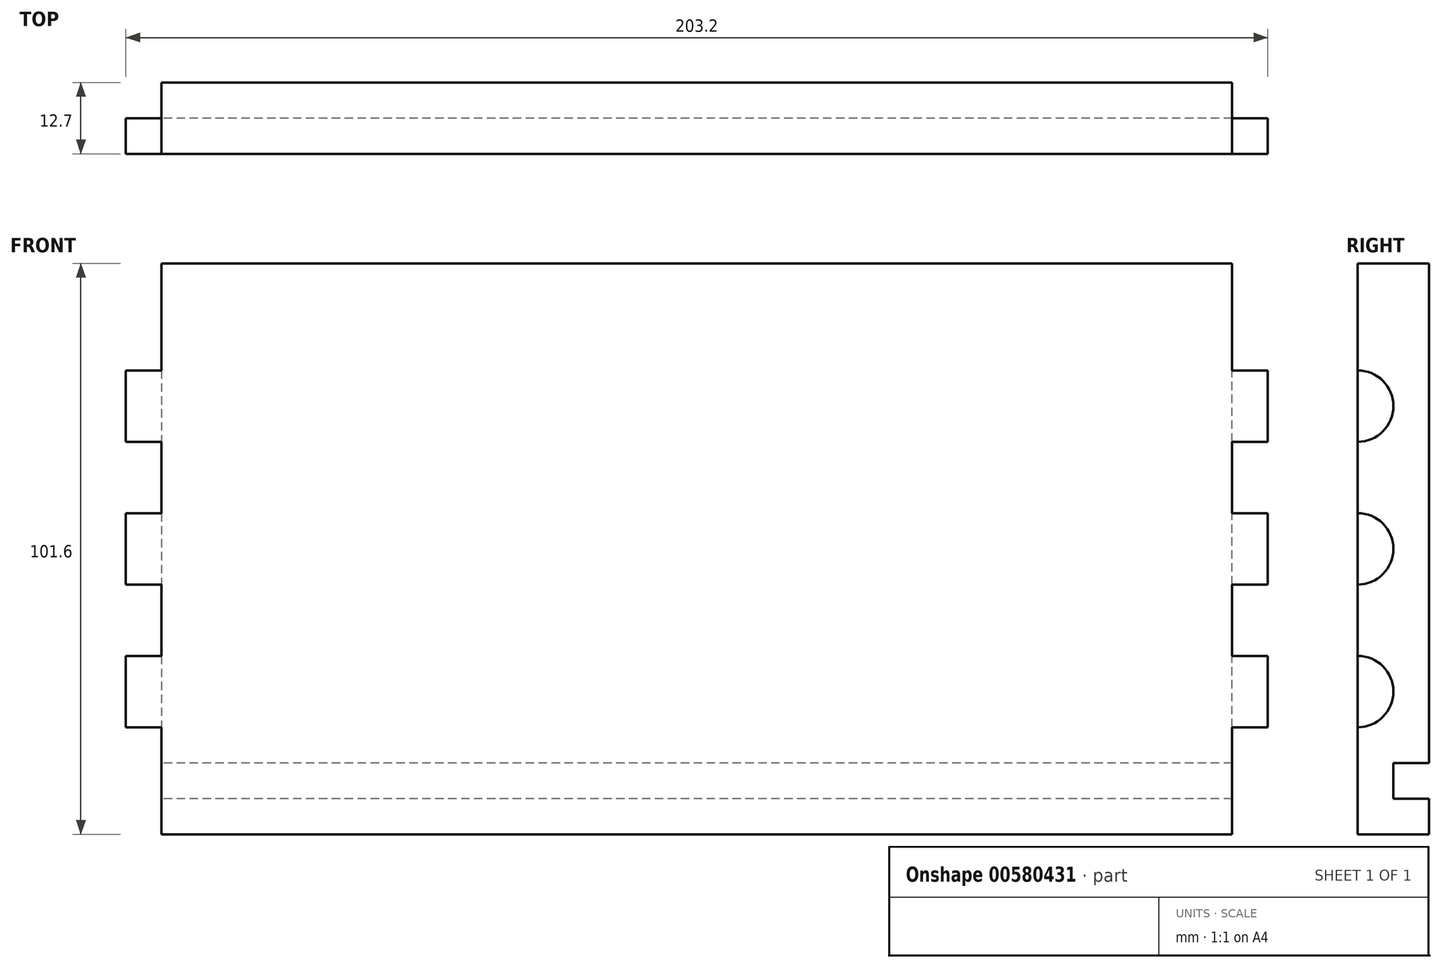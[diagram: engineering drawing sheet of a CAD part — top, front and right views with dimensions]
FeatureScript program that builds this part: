
annotation { "Feature Type Name" : "Feature", "Feature Type Description" : "" }
export const myFeature = defineFeature(function(context is Context, id is Id, definition is map)
    precondition{}
    {
        {
            var Q0;
            Q0=qCreatedBy(makeId("Front.planeOp"),FACE);
            var sketch = newSketch(context, id + "F0", { "sketchPlane" : qUnion([Q0])});
            skLineSegment(sketch, "E0.bottom", {"start": v(-101.6, 50.8) * mm, "end": v(101.6, 50.8) * mm});
            skLineSegment(sketch, "E0.top", {"start": v(-101.6, -50.8) * mm, "end": v(101.6, -50.8) * mm});
            skLineSegment(sketch, "E0.left", {"start": v(-101.6, 50.8) * mm, "end": v(-101.6, -50.8) * mm});
            skLineSegment(sketch, "E0.right", {"start": v(101.6, 50.8) * mm, "end": v(101.6, -50.8) * mm});
            skPoint(sketch, "E0.middle", {"position": v(0, 0) * mm});
            skLineSegment(sketch, "E1.left", {"start": v(101.6, -38.1) * mm, "end": v(101.6, -44.45) * mm});
            skLineSegment(sketch, "E1.right", {"start": v(-101.6, -38.1) * mm, "end": v(-101.6, -44.45) * mm});
            skSolve(sketch);
        }
        {
            var Q0;
            {var subQ3=sQuery(id+"F0.wireOp",EDGE,"E0.bottom");Q0=makeQuery(id+"F0.imprint","IMPRINT",FACE,{"disambiguationData":[TD([[makeQuery(id+"F0.imprint","IMPRINT",EDGE,{"derivedFrom":subQ3}),-1.0]])]});}
            extrude(context, id + "F1", {"entities" : qUnion([Q0]), "depth" : 12.7 * mm, "offsetDistance" : 25.4 * mm});
        }
        {
            var Q0;
            Q0=makeQuery(id+"F1.opExtrude","CAP_FACE",FACE,{"disambiguationData":[OSD([sQuery(id+"F0.wireOp",EDGE,"E0.bottom"),sQuery(id+"F0.wireOp",EDGE,"E0.top"),sQuery(id+"F0.wireOp",EDGE,"E0.left"),sQuery(id+"F0.wireOp",EDGE,"E0.right"),sQuery(id+"F0.wireOp",EDGE,"E1.left"),sQuery(id+"F0.wireOp",EDGE,"E1.right")])],"isStart":true});
            var sketch = newSketch(context, id + "F2", { "sketchPlane" : qUnion([Q0])});
            skLineSegment(sketch, "E2.bottom", {"start": v(-101.6, -38.1) * mm, "end": v(101.6, -38.1) * mm});
            skLineSegment(sketch, "E2.top", {"start": v(-101.6, -44.45) * mm, "end": v(101.6, -44.45) * mm});
            skLineSegment(sketch, "E2.left", {"start": v(-101.6, -38.1) * mm, "end": v(-101.6, -44.45) * mm});
            skLineSegment(sketch, "E2.right", {"start": v(101.6, -38.1) * mm, "end": v(101.6, -44.45) * mm});
            skSolve(sketch);
        }
        {
            var Q0;
            Q0=makeQuery(id+"F2.imprint","IMPRINT",FACE,{"disambiguationData":[TD([[makeQuery(id+"F2.imprint","IMPRINT",EDGE,{"derivedFrom":sQuery(id+"F2.wireOp",EDGE,"E2.bottom")}),-1.0]])]});
            extrude(context, id + "F3", {"entities" : qUnion([Q0]), "operationType" : NewBodyOperationType.REMOVE, "oppositeDirection" : true, "depth" : 6.35 * mm, "offsetDistance" : 25.4 * mm});
        }
        {
            var Q0;
            Q0=makeQuery(id+"F1.opExtrude","SWEPT_FACE",FACE,{"disambiguationData":[OSD([sQuery(id+"F0.wireOp",EDGE,"E0.left"),sQuery(id+"F0.wireOp",EDGE,"E1.right")])]});
            var sketch = newSketch(context, id + "F4", { "sketchPlane" : qUnion([Q0])});
            skArc(sketch, "E3", {"start": v(12.7, 31.75) * mm, "mid": v(6.35, 25.4) * mm, "end": v(12.7, 19.05) * mm});
            skArc(sketch, "E4", {"start": v(12.7, 6.35) * mm, "mid": v(6.35, 0) * mm, "end": v(12.7, -6.35) * mm});
            skArc(sketch, "E5", {"start": v(12.7, -19.05) * mm, "mid": v(6.35, -25.4) * mm, "end": v(12.7, -31.75) * mm});
            skSolve(sketch);
        }
        {
            var Q0;
            Q0 = qSketchRegion(id + "F4", true);
            var Q1;
            {var subQ11=sQuery(id+"F4.wireOp",EDGE,"E3");Q1=makeQuery(id+"F4.imprint","IMPRINT",FACE,{"disambiguationData":[TD([[makeQuery(id+"F4.imprint","IMPRINT",EDGE,{"derivedFrom":subQ11}),-1.0]])]});}
            extrude(context, id + "F5", {"entities" : qUnion([Q0, Q1]), "operationType" : NewBodyOperationType.REMOVE, "oppositeDirection" : true, "depth" : 6.35 * mm, "offsetDistance" : 25.4 * mm});
        }
        {
            var Q0;
            Q0=makeQuery(id+"F1.opExtrude","SWEPT_FACE",FACE,{"disambiguationData":[OSD([sQuery(id+"F0.wireOp",EDGE,"E0.right"),sQuery(id+"F0.wireOp",EDGE,"E1.left")])]});
            var sketch = newSketch(context, id + "F6", { "sketchPlane" : qUnion([Q0])});
            skArc(sketch, "E6", {"start": v(-12.7, 19.05) * mm, "mid": v(-6.35, 25.4) * mm, "end": v(-12.7, 31.75) * mm});
            skArc(sketch, "E7", {"start": v(-12.7, -6.35) * mm, "mid": v(-6.35, 0) * mm, "end": v(-12.7, 6.35) * mm});
            skArc(sketch, "E8", {"start": v(-12.7, -31.75) * mm, "mid": v(-6.35, -25.4) * mm, "end": v(-12.7, -19.05) * mm});
            skSolve(sketch);
        }
        {
            var Q0;
            Q0 = qSketchRegion(id + "F6", true);
            var Q1;
            {var subQ11=sQuery(id+"F6.wireOp",EDGE,"E6");Q1=makeQuery(id+"F6.imprint","IMPRINT",FACE,{"disambiguationData":[TD([[makeQuery(id+"F6.imprint","IMPRINT",EDGE,{"derivedFrom":subQ11}),-1.0]])]});}
            extrude(context, id + "F7", {"entities" : qUnion([Q0, Q1]), "operationType" : NewBodyOperationType.REMOVE, "oppositeDirection" : true, "depth" : 6.35 * mm, "offsetDistance" : 25.4 * mm});
        }
    });
